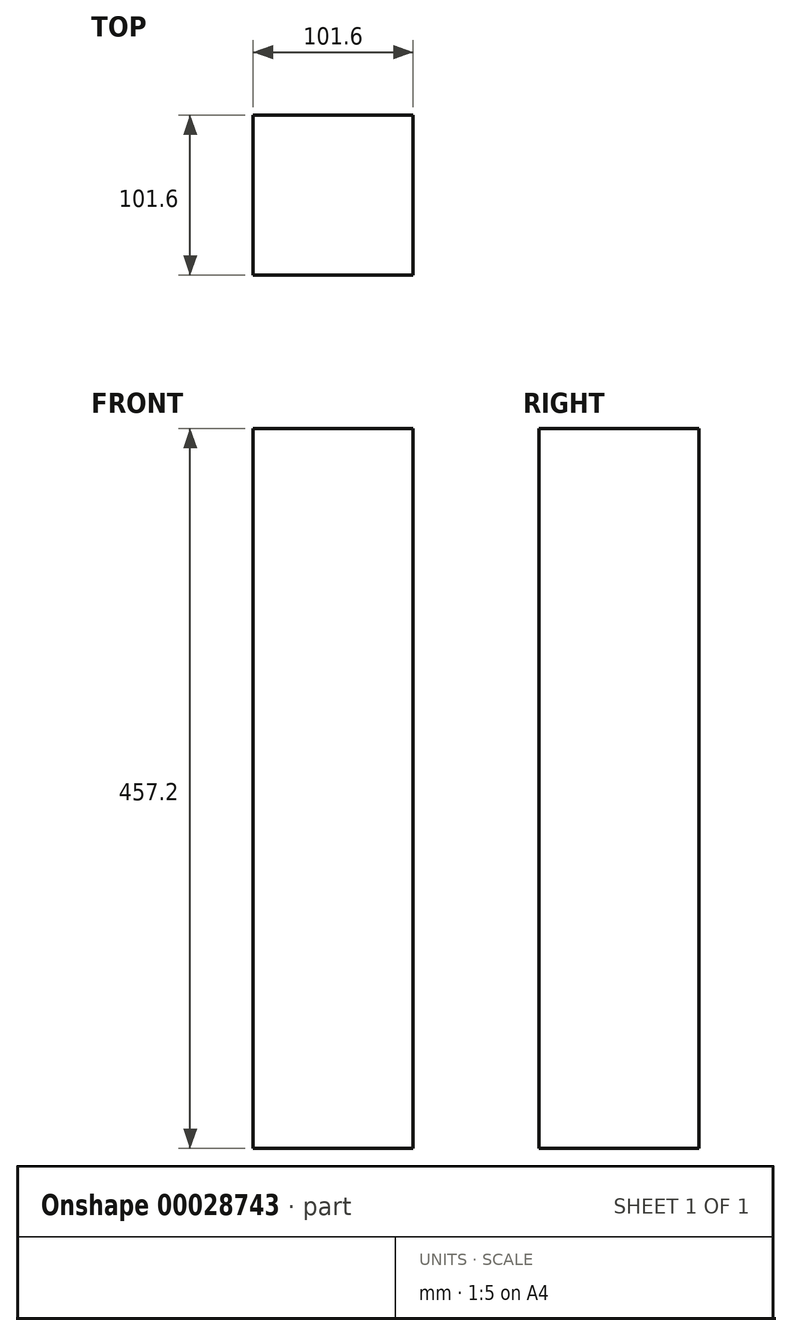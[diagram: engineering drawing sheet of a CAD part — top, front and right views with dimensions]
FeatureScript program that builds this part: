
annotation { "Feature Type Name" : "Feature", "Feature Type Description" : "" }
export const myFeature = defineFeature(function(context is Context, id is Id, definition is map)
    precondition{}
    {
        {
            var Q0;
            Q0=qCreatedBy(makeId("Top.planeOp"),FACE);
            var sketch = newSketch(context, id + "F0", { "sketchPlane" : qUnion([Q0])});
            skLineSegment(sketch, "E0.bottom", {"start": v(-96.61, 82.94) * mm, "end": v(4.99, 82.94) * mm});
            skLineSegment(sketch, "E0.top", {"start": v(-96.61, -18.66) * mm, "end": v(4.99, -18.66) * mm});
            skLineSegment(sketch, "E0.left", {"start": v(-96.61, 82.94) * mm, "end": v(-96.61, -18.66) * mm});
            skLineSegment(sketch, "E0.right", {"start": v(4.99, 82.94) * mm, "end": v(4.99, -18.66) * mm});
            skSolve(sketch);
        }
        {
            var Q0;
            Q0 = qSketchRegion(id + "F0", true);
            extrude(context, id + "F1", {"entities" : qUnion([Q0]), "depth" : 457.2 * mm});
        }
    });
